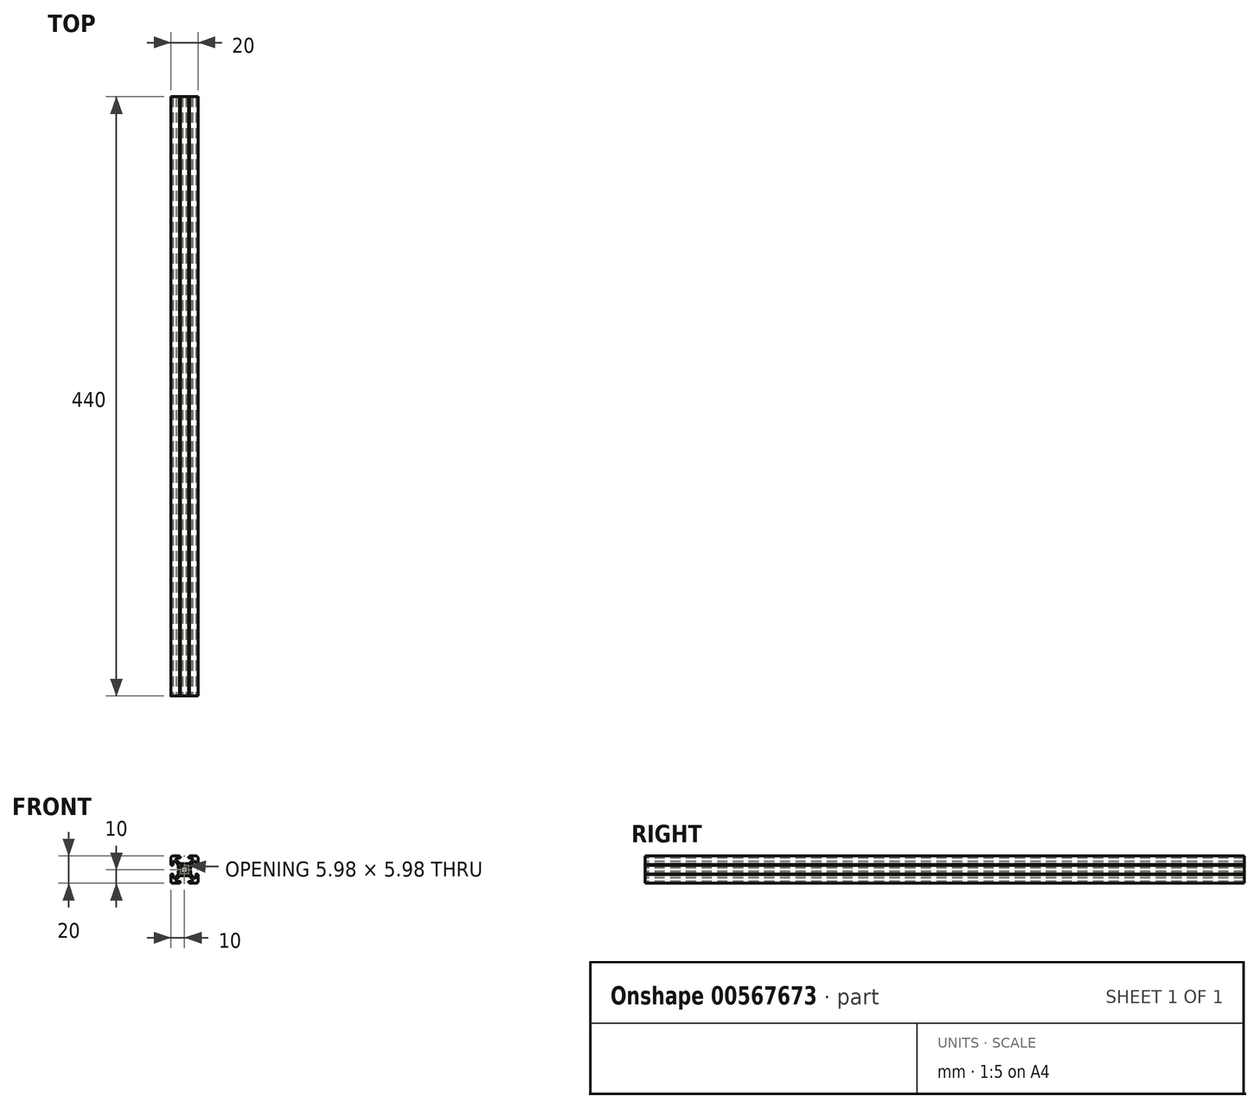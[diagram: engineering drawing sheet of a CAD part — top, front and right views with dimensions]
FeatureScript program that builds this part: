
annotation { "Feature Type Name" : "Feature", "Feature Type Description" : "" }
export const myFeature = defineFeature(function(context is Context, id is Id, definition is map)
    precondition{}
    {
        {
            assignVariable(context, id + "F0", {"name" : "length", "anyValue" : 440});
        }
        {
            var Q0;
            Q0=qCreatedBy(makeId("Front.planeOp"),FACE);
            var sketch = newSketch(context, id + "F1", { "sketchPlane" : qUnion([Q0])});
            skArc(sketch, "E0", {"start": v(8.5, 10) * mm, "mid": v(9.56, 9.56) * mm, "end": v(10, 8.5) * mm});
            skLineSegment(sketch, "E1", {"start": v(3.85, 10) * mm, "end": v(8.5, 10) * mm});
            skArc(sketch, "E2", {"start": v(3.65, 9.8) * mm, "mid": v(3.7, 9.94) * mm, "end": v(3.85, 10) * mm});
            skLineSegment(sketch, "E3", {"start": v(3.65, 9.5) * mm, "end": v(3.65, 9.8) * mm});
            skLineSegment(sketch, "E4", {"start": v(3.3, 9.5) * mm, "end": v(3.65, 9.5) * mm});
            skArc(sketch, "E5", {"start": v(3.1, 9.3) * mm, "mid": v(3.16, 9.44) * mm, "end": v(3.3, 9.5) * mm});
            skLineSegment(sketch, "E6", {"start": v(3.1, 9) * mm, "end": v(3.1, 9.3) * mm});
            skArc(sketch, "E7", {"start": v(3.6, 8.5) * mm, "mid": v(3.25, 8.65) * mm, "end": v(3.1, 9) * mm});
            skLineSegment(sketch, "E8", {"start": v(5.5, 8.5) * mm, "end": v(3.6, 8.5) * mm});
            skArc(sketch, "E9", {"start": v(6, 8) * mm, "mid": v(5.85, 8.35) * mm, "end": v(5.5, 8.5) * mm});
            skLineSegment(sketch, "E10", {"start": v(6, 7.27) * mm, "end": v(6, 8) * mm});
            skArc(sketch, "E11", {"start": v(5.85, 6.91) * mm, "mid": v(5.96, 7.08) * mm, "end": v(6, 7.27) * mm});
            skLineSegment(sketch, "E12", {"start": v(3.59, 4.65) * mm, "end": v(5.85, 6.91) * mm});
            skArc(sketch, "E13", {"start": v(3.23, 4.5) * mm, "mid": v(3.42, 4.54) * mm, "end": v(3.59, 4.65) * mm});
            skLineSegment(sketch, "E14", {"start": v(0.95, 4.5) * mm, "end": v(3.23, 4.5) * mm});
            skArc(sketch, "E15", {"start": v(0.85, 4.47) * mm, "mid": v(0.9, 4.5) * mm, "end": v(0.95, 4.5) * mm});
            skLineSegment(sketch, "E16", {"start": v(0.1, 4.04) * mm, "end": v(0.85, 4.47) * mm});
            skArc(sketch, "E17", {"start": v(-0.1, 4.04) * mm, "mid": v(0, 4.01) * mm, "end": v(0.1, 4.04) * mm});
            skLineSegment(sketch, "E18", {"start": v(-0.85, 4.47) * mm, "end": v(-0.1, 4.04) * mm});
            skArc(sketch, "E19", {"start": v(-0.95, 4.5) * mm, "mid": v(-0.9, 4.5) * mm, "end": v(-0.85, 4.47) * mm});
            skLineSegment(sketch, "E20", {"start": v(-3.23, 4.5) * mm, "end": v(-0.95, 4.5) * mm});
            skArc(sketch, "E21", {"start": v(-3.59, 4.65) * mm, "mid": v(-3.42, 4.54) * mm, "end": v(-3.23, 4.5) * mm});
            skLineSegment(sketch, "E22", {"start": v(-5.85, 6.91) * mm, "end": v(-3.59, 4.65) * mm});
            skArc(sketch, "E23", {"start": v(-6, 7.27) * mm, "mid": v(-5.96, 7.08) * mm, "end": v(-5.85, 6.91) * mm});
            skLineSegment(sketch, "E24", {"start": v(-6, 8) * mm, "end": v(-6, 7.27) * mm});
            skArc(sketch, "E25", {"start": v(-5.5, 8.5) * mm, "mid": v(-5.85, 8.35) * mm, "end": v(-6, 8) * mm});
            skLineSegment(sketch, "E26", {"start": v(-3.6, 8.5) * mm, "end": v(-5.5, 8.5) * mm});
            skArc(sketch, "E27", {"start": v(-3.1, 9) * mm, "mid": v(-3.25, 8.65) * mm, "end": v(-3.6, 8.5) * mm});
            skLineSegment(sketch, "E28", {"start": v(-3.1, 9.3) * mm, "end": v(-3.1, 9) * mm});
            skArc(sketch, "E29", {"start": v(-3.3, 9.5) * mm, "mid": v(-3.16, 9.44) * mm, "end": v(-3.1, 9.3) * mm});
            skLineSegment(sketch, "E30", {"start": v(-3.65, 9.5) * mm, "end": v(-3.3, 9.5) * mm});
            skLineSegment(sketch, "E31", {"start": v(-3.65, 9.8) * mm, "end": v(-3.65, 9.5) * mm});
            skArc(sketch, "E32", {"start": v(-3.85, 10) * mm, "mid": v(-3.7, 9.94) * mm, "end": v(-3.65, 9.8) * mm});
            skLineSegment(sketch, "E33", {"start": v(-8.5, 10) * mm, "end": v(-3.85, 10) * mm});
            skArc(sketch, "E34", {"start": v(-10, 8.5) * mm, "mid": v(-9.56, 9.56) * mm, "end": v(-8.5, 10) * mm});
            skLineSegment(sketch, "E35", {"start": v(-10, 3.85) * mm, "end": v(-10, 8.5) * mm});
            skArc(sketch, "E36", {"start": v(-9.8, 3.65) * mm, "mid": v(-9.94, 3.7) * mm, "end": v(-10, 3.85) * mm});
            skLineSegment(sketch, "E37", {"start": v(-9.5, 3.65) * mm, "end": v(-9.8, 3.65) * mm});
            skLineSegment(sketch, "E38", {"start": v(-9.5, 3.3) * mm, "end": v(-9.5, 3.65) * mm});
            skArc(sketch, "E39", {"start": v(-9.3, 3.1) * mm, "mid": v(-9.44, 3.16) * mm, "end": v(-9.5, 3.3) * mm});
            skLineSegment(sketch, "E40", {"start": v(-9, 3.1) * mm, "end": v(-9.3, 3.1) * mm});
            skArc(sketch, "E41", {"start": v(-8.5, 3.6) * mm, "mid": v(-8.65, 3.25) * mm, "end": v(-9, 3.1) * mm});
            skLineSegment(sketch, "E42", {"start": v(-8.5, 5.5) * mm, "end": v(-8.5, 3.6) * mm});
            skArc(sketch, "E43", {"start": v(-8, 6) * mm, "mid": v(-8.35, 5.85) * mm, "end": v(-8.5, 5.5) * mm});
            skLineSegment(sketch, "E44", {"start": v(-7.27, 6) * mm, "end": v(-8, 6) * mm});
            skArc(sketch, "E45", {"start": v(-6.91, 5.85) * mm, "mid": v(-7.08, 5.96) * mm, "end": v(-7.27, 6) * mm});
            skLineSegment(sketch, "E46", {"start": v(-4.65, 3.59) * mm, "end": v(-6.91, 5.85) * mm});
            skArc(sketch, "E47", {"start": v(-4.5, 3.23) * mm, "mid": v(-4.54, 3.42) * mm, "end": v(-4.65, 3.59) * mm});
            skLineSegment(sketch, "E48", {"start": v(-4.5, 0.95) * mm, "end": v(-4.5, 3.23) * mm});
            skArc(sketch, "E49", {"start": v(-4.47, 0.85) * mm, "mid": v(-4.5, 0.9) * mm, "end": v(-4.5, 0.95) * mm});
            skLineSegment(sketch, "E50", {"start": v(-4.04, 0.1) * mm, "end": v(-4.47, 0.85) * mm});
            skArc(sketch, "E51", {"start": v(-4.04, -0.1) * mm, "mid": v(-4.01, 0) * mm, "end": v(-4.04, 0.1) * mm});
            skLineSegment(sketch, "E52", {"start": v(-4.47, -0.85) * mm, "end": v(-4.04, -0.1) * mm});
            skArc(sketch, "E53", {"start": v(-4.5, -0.95) * mm, "mid": v(-4.5, -0.9) * mm, "end": v(-4.47, -0.85) * mm});
            skLineSegment(sketch, "E54", {"start": v(-4.5, -3.23) * mm, "end": v(-4.5, -0.95) * mm});
            skArc(sketch, "E55", {"start": v(-4.65, -3.59) * mm, "mid": v(-4.54, -3.42) * mm, "end": v(-4.5, -3.23) * mm});
            skLineSegment(sketch, "E56", {"start": v(-6.91, -5.85) * mm, "end": v(-4.65, -3.59) * mm});
            skArc(sketch, "E57", {"start": v(-7.27, -6) * mm, "mid": v(-7.08, -5.96) * mm, "end": v(-6.91, -5.85) * mm});
            skLineSegment(sketch, "E58", {"start": v(-8, -6) * mm, "end": v(-7.27, -6) * mm});
            skArc(sketch, "E59", {"start": v(-8.5, -5.5) * mm, "mid": v(-8.35, -5.85) * mm, "end": v(-8, -6) * mm});
            skLineSegment(sketch, "E60", {"start": v(-8.5, -3.6) * mm, "end": v(-8.5, -5.5) * mm});
            skArc(sketch, "E61", {"start": v(-9, -3.1) * mm, "mid": v(-8.65, -3.25) * mm, "end": v(-8.5, -3.6) * mm});
            skLineSegment(sketch, "E62", {"start": v(-9.3, -3.1) * mm, "end": v(-9, -3.1) * mm});
            skArc(sketch, "E63", {"start": v(-9.5, -3.3) * mm, "mid": v(-9.44, -3.16) * mm, "end": v(-9.3, -3.1) * mm});
            skLineSegment(sketch, "E64", {"start": v(-9.5, -3.65) * mm, "end": v(-9.5, -3.3) * mm});
            skLineSegment(sketch, "E65", {"start": v(-9.8, -3.65) * mm, "end": v(-9.5, -3.65) * mm});
            skArc(sketch, "E66", {"start": v(-10, -3.85) * mm, "mid": v(-9.94, -3.7) * mm, "end": v(-9.8, -3.65) * mm});
            skLineSegment(sketch, "E67", {"start": v(-10, -8.5) * mm, "end": v(-10, -3.85) * mm});
            skArc(sketch, "E68", {"start": v(-8.5, -10) * mm, "mid": v(-9.56, -9.56) * mm, "end": v(-10, -8.5) * mm});
            skLineSegment(sketch, "E69", {"start": v(-3.85, -10) * mm, "end": v(-8.5, -10) * mm});
            skArc(sketch, "E70", {"start": v(-3.65, -9.8) * mm, "mid": v(-3.7, -9.94) * mm, "end": v(-3.85, -10) * mm});
            skLineSegment(sketch, "E71", {"start": v(-3.65, -9.5) * mm, "end": v(-3.65, -9.8) * mm});
            skLineSegment(sketch, "E72", {"start": v(-3.3, -9.5) * mm, "end": v(-3.65, -9.5) * mm});
            skArc(sketch, "E73", {"start": v(-3.1, -9.3) * mm, "mid": v(-3.16, -9.44) * mm, "end": v(-3.3, -9.5) * mm});
            skLineSegment(sketch, "E74", {"start": v(-3.1, -9) * mm, "end": v(-3.1, -9.3) * mm});
            skArc(sketch, "E75", {"start": v(-3.6, -8.5) * mm, "mid": v(-3.25, -8.65) * mm, "end": v(-3.1, -9) * mm});
            skLineSegment(sketch, "E76", {"start": v(-5.5, -8.5) * mm, "end": v(-3.6, -8.5) * mm});
            skArc(sketch, "E77", {"start": v(-6, -8) * mm, "mid": v(-5.85, -8.35) * mm, "end": v(-5.5, -8.5) * mm});
            skLineSegment(sketch, "E78", {"start": v(-6, -7.27) * mm, "end": v(-6, -8) * mm});
            skArc(sketch, "E79", {"start": v(-5.85, -6.91) * mm, "mid": v(-5.96, -7.08) * mm, "end": v(-6, -7.27) * mm});
            skLineSegment(sketch, "E80", {"start": v(-3.59, -4.65) * mm, "end": v(-5.85, -6.91) * mm});
            skArc(sketch, "E81", {"start": v(-3.23, -4.5) * mm, "mid": v(-3.42, -4.54) * mm, "end": v(-3.59, -4.65) * mm});
            skLineSegment(sketch, "E82", {"start": v(-0.95, -4.5) * mm, "end": v(-3.23, -4.5) * mm});
            skArc(sketch, "E83", {"start": v(-0.85, -4.47) * mm, "mid": v(-0.9, -4.5) * mm, "end": v(-0.95, -4.5) * mm});
            skLineSegment(sketch, "E84", {"start": v(-0.1, -4.04) * mm, "end": v(-0.85, -4.47) * mm});
            skArc(sketch, "E85", {"start": v(0.1, -4.04) * mm, "mid": v(0, -4.01) * mm, "end": v(-0.1, -4.04) * mm});
            skLineSegment(sketch, "E86", {"start": v(0.85, -4.47) * mm, "end": v(0.1, -4.04) * mm});
            skArc(sketch, "E87", {"start": v(0.95, -4.5) * mm, "mid": v(0.9, -4.5) * mm, "end": v(0.85, -4.47) * mm});
            skLineSegment(sketch, "E88", {"start": v(3.23, -4.5) * mm, "end": v(0.95, -4.5) * mm});
            skArc(sketch, "E89", {"start": v(3.59, -4.65) * mm, "mid": v(3.42, -4.54) * mm, "end": v(3.23, -4.5) * mm});
            skLineSegment(sketch, "E90", {"start": v(5.85, -6.91) * mm, "end": v(3.59, -4.65) * mm});
            skArc(sketch, "E91", {"start": v(6, -7.27) * mm, "mid": v(5.96, -7.08) * mm, "end": v(5.85, -6.91) * mm});
            skLineSegment(sketch, "E92", {"start": v(6, -8) * mm, "end": v(6, -7.27) * mm});
            skArc(sketch, "E93", {"start": v(5.5, -8.5) * mm, "mid": v(5.85, -8.35) * mm, "end": v(6, -8) * mm});
            skLineSegment(sketch, "E94", {"start": v(3.6, -8.5) * mm, "end": v(5.5, -8.5) * mm});
            skArc(sketch, "E95", {"start": v(3.1, -9) * mm, "mid": v(3.25, -8.65) * mm, "end": v(3.6, -8.5) * mm});
            skLineSegment(sketch, "E96", {"start": v(3.1, -9.3) * mm, "end": v(3.1, -9) * mm});
            skArc(sketch, "E97", {"start": v(3.3, -9.5) * mm, "mid": v(3.16, -9.44) * mm, "end": v(3.1, -9.3) * mm});
            skLineSegment(sketch, "E98", {"start": v(3.65, -9.5) * mm, "end": v(3.3, -9.5) * mm});
            skLineSegment(sketch, "E99", {"start": v(3.65, -9.8) * mm, "end": v(3.65, -9.5) * mm});
            skArc(sketch, "E100", {"start": v(3.85, -10) * mm, "mid": v(3.7, -9.94) * mm, "end": v(3.65, -9.8) * mm});
            skLineSegment(sketch, "E101", {"start": v(8.5, -10) * mm, "end": v(3.85, -10) * mm});
            skArc(sketch, "E102", {"start": v(10, -8.5) * mm, "mid": v(9.56, -9.56) * mm, "end": v(8.5, -10) * mm});
            skLineSegment(sketch, "E103", {"start": v(10, -3.85) * mm, "end": v(10, -8.5) * mm});
            skArc(sketch, "E104", {"start": v(9.8, -3.65) * mm, "mid": v(9.94, -3.7) * mm, "end": v(10, -3.85) * mm});
            skLineSegment(sketch, "E105", {"start": v(9.5, -3.65) * mm, "end": v(9.8, -3.65) * mm});
            skLineSegment(sketch, "E106", {"start": v(9.5, -3.3) * mm, "end": v(9.5, -3.65) * mm});
            skArc(sketch, "E107", {"start": v(9.3, -3.1) * mm, "mid": v(9.44, -3.16) * mm, "end": v(9.5, -3.3) * mm});
            skLineSegment(sketch, "E108", {"start": v(9, -3.1) * mm, "end": v(9.3, -3.1) * mm});
            skArc(sketch, "E109", {"start": v(8.5, -3.6) * mm, "mid": v(8.65, -3.25) * mm, "end": v(9, -3.1) * mm});
            skLineSegment(sketch, "E110", {"start": v(8.5, -5.5) * mm, "end": v(8.5, -3.6) * mm});
            skArc(sketch, "E111", {"start": v(8, -6) * mm, "mid": v(8.35, -5.85) * mm, "end": v(8.5, -5.5) * mm});
            skLineSegment(sketch, "E112", {"start": v(7.27, -6) * mm, "end": v(8, -6) * mm});
            skArc(sketch, "E113", {"start": v(6.91, -5.85) * mm, "mid": v(7.08, -5.96) * mm, "end": v(7.27, -6) * mm});
            skLineSegment(sketch, "E114", {"start": v(4.65, -3.59) * mm, "end": v(6.91, -5.85) * mm});
            skArc(sketch, "E115", {"start": v(4.5, -3.23) * mm, "mid": v(4.54, -3.42) * mm, "end": v(4.65, -3.59) * mm});
            skLineSegment(sketch, "E116", {"start": v(4.5, -0.95) * mm, "end": v(4.5, -3.23) * mm});
            skArc(sketch, "E117", {"start": v(4.47, -0.85) * mm, "mid": v(4.5, -0.9) * mm, "end": v(4.5, -0.95) * mm});
            skLineSegment(sketch, "E118", {"start": v(4.04, -0.1) * mm, "end": v(4.47, -0.85) * mm});
            skArc(sketch, "E119", {"start": v(4.04, 0.1) * mm, "mid": v(4.01, 0) * mm, "end": v(4.04, -0.1) * mm});
            skLineSegment(sketch, "E120", {"start": v(4.47, 0.85) * mm, "end": v(4.04, 0.1) * mm});
            skArc(sketch, "E121", {"start": v(4.5, 0.95) * mm, "mid": v(4.5, 0.9) * mm, "end": v(4.47, 0.85) * mm});
            skLineSegment(sketch, "E122", {"start": v(4.5, 3.23) * mm, "end": v(4.5, 0.95) * mm});
            skArc(sketch, "E123", {"start": v(4.65, 3.59) * mm, "mid": v(4.54, 3.42) * mm, "end": v(4.5, 3.23) * mm});
            skLineSegment(sketch, "E124", {"start": v(6.91, 5.85) * mm, "end": v(4.65, 3.59) * mm});
            skArc(sketch, "E125", {"start": v(7.27, 6) * mm, "mid": v(7.08, 5.96) * mm, "end": v(6.91, 5.85) * mm});
            skLineSegment(sketch, "E126", {"start": v(8, 6) * mm, "end": v(7.27, 6) * mm});
            skArc(sketch, "E127", {"start": v(8.5, 5.5) * mm, "mid": v(8.35, 5.85) * mm, "end": v(8, 6) * mm});
            skLineSegment(sketch, "E128", {"start": v(8.5, 3.6) * mm, "end": v(8.5, 5.5) * mm});
            skArc(sketch, "E129", {"start": v(9, 3.1) * mm, "mid": v(8.65, 3.25) * mm, "end": v(8.5, 3.6) * mm});
            skLineSegment(sketch, "E130", {"start": v(9.3, 3.1) * mm, "end": v(9, 3.1) * mm});
            skArc(sketch, "E131", {"start": v(9.5, 3.3) * mm, "mid": v(9.44, 3.16) * mm, "end": v(9.3, 3.1) * mm});
            skLineSegment(sketch, "E132", {"start": v(9.5, 3.65) * mm, "end": v(9.5, 3.3) * mm});
            skLineSegment(sketch, "E133", {"start": v(9.8, 3.65) * mm, "end": v(9.5, 3.65) * mm});
            skArc(sketch, "E134", {"start": v(10, 3.85) * mm, "mid": v(9.94, 3.7) * mm, "end": v(9.8, 3.65) * mm});
            skLineSegment(sketch, "E135", {"start": v(10, 8.5) * mm, "end": v(10, 3.85) * mm});
            skArc(sketch, "E136", {"start": v(1.91, 2.99) * mm, "mid": v(2.51, 2.5) * mm, "end": v(3, 1.9) * mm});
            skLineSegment(sketch, "E137", {"start": v(1.26, 2.45) * mm, "end": v(1.91, 2.99) * mm});
            skArc(sketch, "E138", {"start": v(-1.26, 2.45) * mm, "mid": v(0, 2.75) * mm, "end": v(1.26, 2.45) * mm});
            skLineSegment(sketch, "E139", {"start": v(-1.91, 2.99) * mm, "end": v(-1.26, 2.45) * mm});
            skArc(sketch, "E140", {"start": v(-3, 1.9) * mm, "mid": v(-2.51, 2.5) * mm, "end": v(-1.91, 2.99) * mm});
            skLineSegment(sketch, "E141", {"start": v(-2.45, 1.26) * mm, "end": v(-3, 1.9) * mm});
            skArc(sketch, "E142", {"start": v(-2.45, -1.26) * mm, "mid": v(-2.75, 0) * mm, "end": v(-2.45, 1.26) * mm});
            skLineSegment(sketch, "E143", {"start": v(-3, -1.9) * mm, "end": v(-2.45, -1.26) * mm});
            skArc(sketch, "E144", {"start": v(-1.91, -2.99) * mm, "mid": v(-2.51, -2.5) * mm, "end": v(-3, -1.9) * mm});
            skLineSegment(sketch, "E145", {"start": v(-1.26, -2.45) * mm, "end": v(-1.91, -2.99) * mm});
            skArc(sketch, "E146", {"start": v(1.26, -2.45) * mm, "mid": v(0, -2.75) * mm, "end": v(-1.26, -2.45) * mm});
            skLineSegment(sketch, "E147", {"start": v(1.91, -2.99) * mm, "end": v(1.26, -2.45) * mm});
            skArc(sketch, "E148", {"start": v(3, -1.9) * mm, "mid": v(2.51, -2.5) * mm, "end": v(1.91, -2.99) * mm});
            skLineSegment(sketch, "E149", {"start": v(2.45, -1.26) * mm, "end": v(3, -1.9) * mm});
            skArc(sketch, "E150", {"start": v(2.45, 1.26) * mm, "mid": v(2.75, 0) * mm, "end": v(2.45, -1.26) * mm});
            skLineSegment(sketch, "E151", {"start": v(3, 1.9) * mm, "end": v(2.45, 1.26) * mm});
            skSolve(sketch);
        }
        {
            var Q0;
            Q0 = qSketchRegion(id + "F1", true);
            extrude(context, id + "F2", {"entities" : qUnion([Q0]), "oppositeDirection" : true, "depth" : (getVariable(context, 'length')) * mm, "offsetDistance" : 25 * mm});
        }
    });
